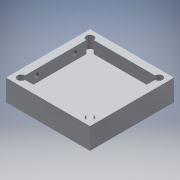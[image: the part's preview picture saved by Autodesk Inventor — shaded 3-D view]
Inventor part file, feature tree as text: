
AUTODESK INVENTOR PART (.ipt)
format: ipt  version: 2017 (Build 210142000, 142)  size: 160,256 bytes
history: native  units: mm
features: sketch x7, hole x4, extrude x3, projected_geometry x3, other x1, split x1
ambient origin geometry x8: Origin, YZ Plane, XZ Plane, XY Plane, X Axis, Y Axis, Z Axis, Center Point
bodies: Body1 (feature_tree)
feature tree (19):
  extrude  "Extrusion1"  Depth=55.0mm
  hole  "Hole2"  [1 undecoded]
  extrude  "Extrusion3"  Depth=8.0mm TaperAngle=0.0deg
  hole  "Hole3"  [1 undecoded]
  extrude  "Extrusion4"  Depth=8.0mm
  hole  "Hole5"  [1 undecoded]
  hole  "Hole6"  [1 undecoded]
  other  "SplitPLane"
  split  "Split2"
  sketch  "Sketch1"  dims[d0=55.0mm d1=55.0mm]
  sketch  "Sketch4"  dims[d2=20.0mm d3=0.0mm d15=45.1mm]
  sketch  "Sketch5"  dims[d16=45.1mm]
  sketch  "Sketch6"  dims[d17=5.0mm d18=6.0mm d19=4.0mm d20=2.0mm d21=90.0deg d22=8.0mm d23=0.0mm d24=8.0mm d25=0.0mm]
  projected_geometry  "Projected Loop1"
  sketch  "Sketch8"  dims[d26=15.0mm d27=15.0mm]
  projected_geometry  "Projected Loop2"
  sketch  "Sketch9"  dims[d28=3.242mm d29=6.0mm d30=4.0mm d31=2.0mm d32=90.0deg d33=8.0mm d34=20.594885mm d44=25.0mm]
  projected_geometry  "Projected Loop3"
  sketch  "Sketch10"  dims[d45=25.0mm d46=6.0mm d47=0.0mm d48=3.0mm d49=6.0mm d50=4.0mm d51=2.0mm d52=90.0deg d53=6.0mm d54=0.0mm d55=3.242mm d56=8.0mm d57=4.0mm d58=2.0mm d59=90.0deg d60=4.0mm d61=20.594885mm d62=0.0mm]
note: 4 required parameter values undecoded (feature->parameter linkage not recoverable at this tier; creation-order binding heuristic only, values carry confidence <= 0.55)
